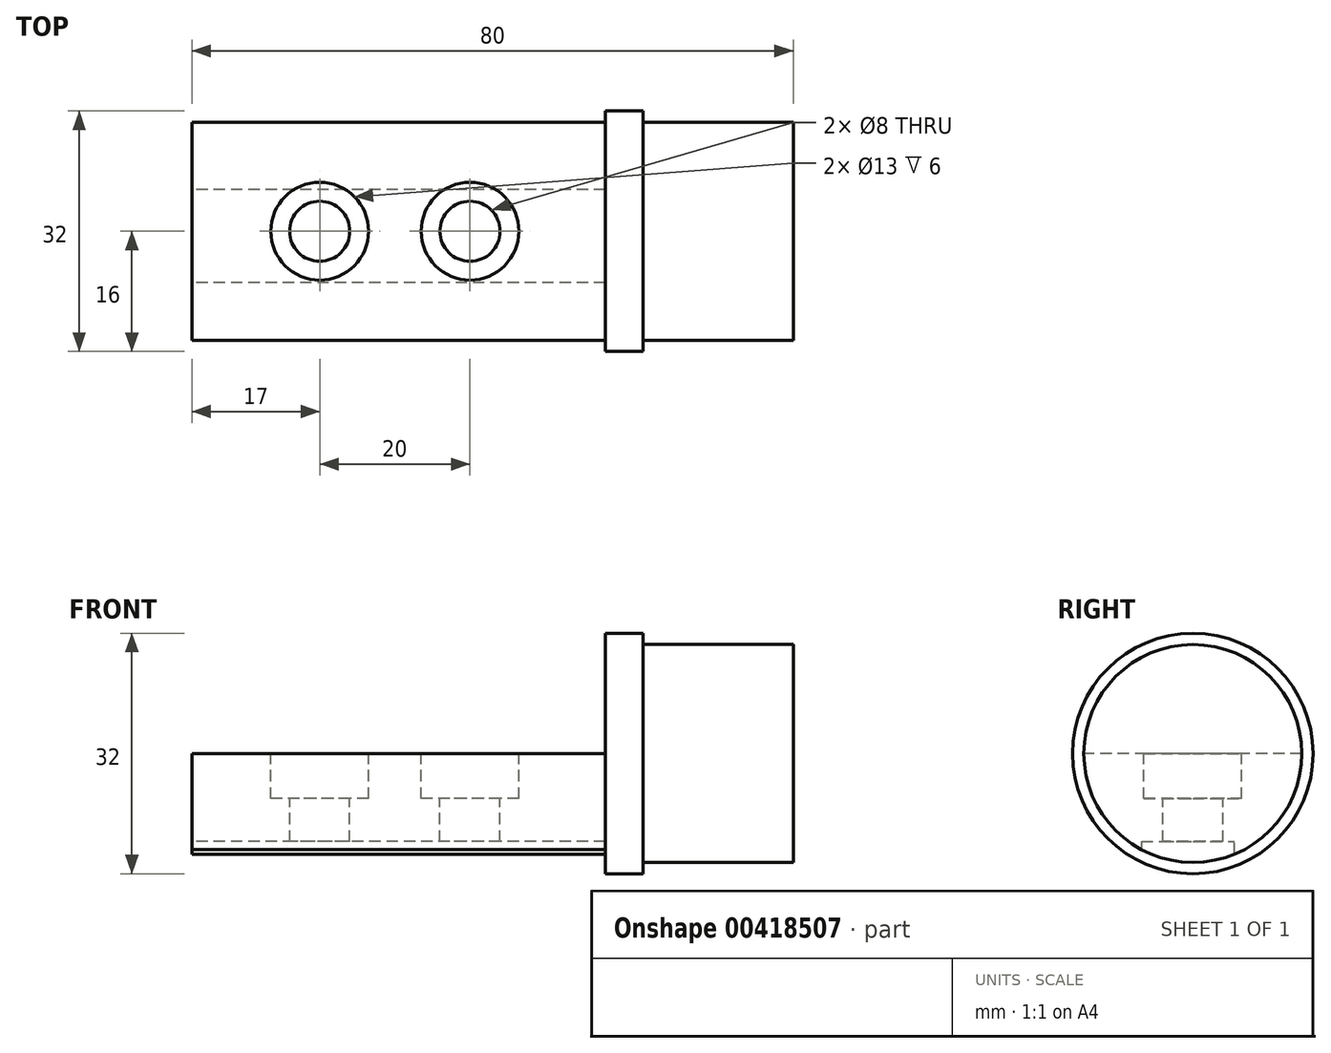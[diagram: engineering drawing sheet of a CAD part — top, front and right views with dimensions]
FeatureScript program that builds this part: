
annotation { "Feature Type Name" : "Feature", "Feature Type Description" : "" }
export const myFeature = defineFeature(function(context is Context, id is Id, definition is map)
    precondition{}
    {
        {
            var Q0;
            Q0=qCreatedBy(makeId("Front.planeOp"),FACE);
            var sketch = newSketch(context, id + "F0", { "sketchPlane" : qUnion([Q0])});
            skLineSegment(sketch, "E0", {"start": v(-55, 14.5) * mm, "end": v(0, 14.5) * mm});
            skLineSegment(sketch, "E1", {"start": v(0, 16) * mm, "end": v(5, 16) * mm});
            skLineSegment(sketch, "E2", {"start": v(5, 16) * mm, "end": v(5, 14.5) * mm});
            skLineSegment(sketch, "E3", {"start": v(5, 14.5) * mm, "end": v(25, 14.5) * mm});
            skLineSegment(sketch, "E4", {"start": v(25, 14.5) * mm, "end": v(25, 0) * mm});
            skLineSegment(sketch, "E5", {"start": v(25, 0) * mm, "end": v(-55, 0) * mm});
            skLineSegment(sketch, "E6", {"start": v(-55, 0) * mm, "end": v(-55, 14.5) * mm});
            skLineSegment(sketch, "E7", {"start": v(0, 16) * mm, "end": v(0, 0) * mm});
            skSolve(sketch);
        }
        {
            var Q0;
            Q0 = qSketchRegion(id + "F0", true);
            var Q1;
            Q1=sQuery(id+"F0.wireOp",EDGE,"E5");
            revolve(context, id + "F1", {"entities" : qUnion([Q0]), "axis" : qUnion([Q1]), "revolveType" : RevolveType.FULL});
        }
        {
            var Q0;
            Q0=makeQuery(id+"F1.opRevolve","SWEPT_FACE",FACE,{"disambiguationData":[OSD([sQuery(id+"F0.wireOp",EDGE,"E6")])]});
            var sketch = newSketch(context, id + "F2", { "sketchPlane" : qUnion([Q0])});
            skLineSegment(sketch, "E8", {"start": v(-14.5, 0) * mm, "end": v(14.5, 0) * mm});
            skSolve(sketch);
        }
        {
            var Q0;
            Q0 = qSketchRegion(id + "F2", true);
            var Q1;
            {var subQ0=sQuery(id+"F2.wireOp",EDGE,"E8");Q1=makeQuery(id+"F2.imprint","IMPRINT",FACE,{"disambiguationData":[TD([[makeQuery(id+"F2.imprint","IMPRINT",EDGE,{"derivedFrom":subQ0}),1.0]])]});}
            extrude(context, id + "F3", {"entities" : qUnion([Q0, Q1]), "operationType" : NewBodyOperationType.REMOVE, "oppositeDirection" : true, "depth" : 55 * mm});
        }
        {
            var Q0;
            Q0=makeQuery(id+"F3.boolean.opBoolean","COPY",FACE,{"derivedFrom":makeQuery(id+"F3.opExtrude","SWEPT_FACE",FACE,{"disambiguationData":[OSD([sQuery(id+"F2.wireOp",EDGE,"E8")])]})});
            var sketch = newSketch(context, id + "F4", { "sketchPlane" : qUnion([Q0])});
            skCircle(sketch, "E9", {"center": v(-38, 0) * mm, "radius": 4 * mm});
            skCircle(sketch, "E10", {"center": v(-18, 0) * mm, "radius": 4 * mm});
            skCircle(sketch, "E11", {"center": v(-38, 0) * mm, "radius": 6.5 * mm});
            skCircle(sketch, "E12", {"center": v(-18, 0) * mm, "radius": 6.5 * mm});
            skSolve(sketch);
        }
        {
            var Q0;
            Q0=makeQuery(id+"F4.imprint","IMPRINT",FACE,{"disambiguationData":[TD([[makeQuery(id+"F4.imprint","IMPRINT",EDGE,{"derivedFrom":sQuery(id+"F4.wireOp",EDGE,"E9")}),1.0]])]});
            var Q1;
            Q1=makeQuery(id+"F4.imprint","IMPRINT",FACE,{"disambiguationData":[TD([[makeQuery(id+"F4.imprint","IMPRINT",EDGE,{"derivedFrom":sQuery(id+"F4.wireOp",EDGE,"E10")}),1.0]])]});
            extrude(context, id + "F5", {"entities" : qUnion([Q0, Q1]), "operationType" : NewBodyOperationType.REMOVE, "endBound" : BoundingType.THROUGH_ALL, "oppositeDirection" : true, "depth" : 25 * mm});
        }
        {
            var Q0;
            {var subQ0=sQuery(id+"F2.wireOp",EDGE,"E8");Q0=makeQuery(id+"F2.imprint","IMPRINT",FACE,{"disambiguationData":[TD([[makeQuery(id+"F2.imprint","IMPRINT",EDGE,{"derivedFrom":subQ0}),-1.0]])]});}
            var sketch = newSketch(context, id + "F6", { "sketchPlane" : qUnion([Q0])});
            skLineSegment(sketch, "E13.bottom", {"start": v(6.81, -14.74) * mm, "end": v(-5.55, -14.74) * mm});
            skLineSegment(sketch, "E13.top", {"start": v(6.81, -11.71) * mm, "end": v(-5.55, -11.71) * mm});
            skLineSegment(sketch, "E13.left", {"start": v(6.81, -14.74) * mm, "end": v(6.81, -11.71) * mm});
            skLineSegment(sketch, "E13.right", {"start": v(-5.55, -14.74) * mm, "end": v(-5.55, -11.71) * mm});
            skSolve(sketch);
        }
        {
            var Q0;
            {var subQ0=sQuery(id+"F6.wireOp",EDGE,"E13.top");Q0=makeQuery(id+"F6.imprint","IMPRINT",FACE,{"disambiguationData":[TD([[makeQuery(id+"F6.imprint","IMPRINT",EDGE,{"derivedFrom":subQ0}),1.0]])]});}
            extrude(context, id + "F7", {"entities" : qUnion([Q0]), "operationType" : NewBodyOperationType.REMOVE, "oppositeDirection" : true, "depth" : 55 * mm});
        }
        {
            var Q0;
            Q0 = qSketchRegion(id + "F4", true);
            extrude(context, id + "F8", {"entities" : qUnion([Q0]), "operationType" : NewBodyOperationType.REMOVE, "oppositeDirection" : true, "depth" : 6 * mm});
        }
    });
